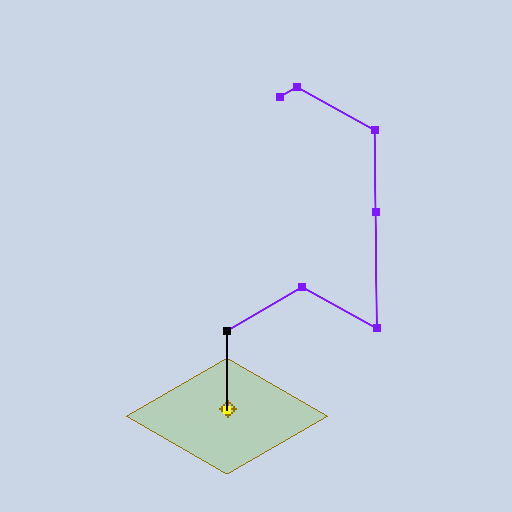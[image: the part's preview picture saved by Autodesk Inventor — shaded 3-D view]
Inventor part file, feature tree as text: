
AUTODESK INVENTOR PART (.ipt)
format: ipt  version: 2025 (Build 290162000, 162)  size: 103,936 bytes
history: native  units: in
note: dims shown in document units (in); Inventor stores cm internally (conversion verified against a paired STEP export)
features: other x1, plane x1, sketch x1
ambient origin geometry x8: Origin, YZ Plane, XZ Plane, XY Plane, X Axis, Y Axis, Z Axis, Center Point
feature tree (3):
  other  "Work Point1"
  plane  "Work Plane1"
  sketch  "3D Sketch1"
